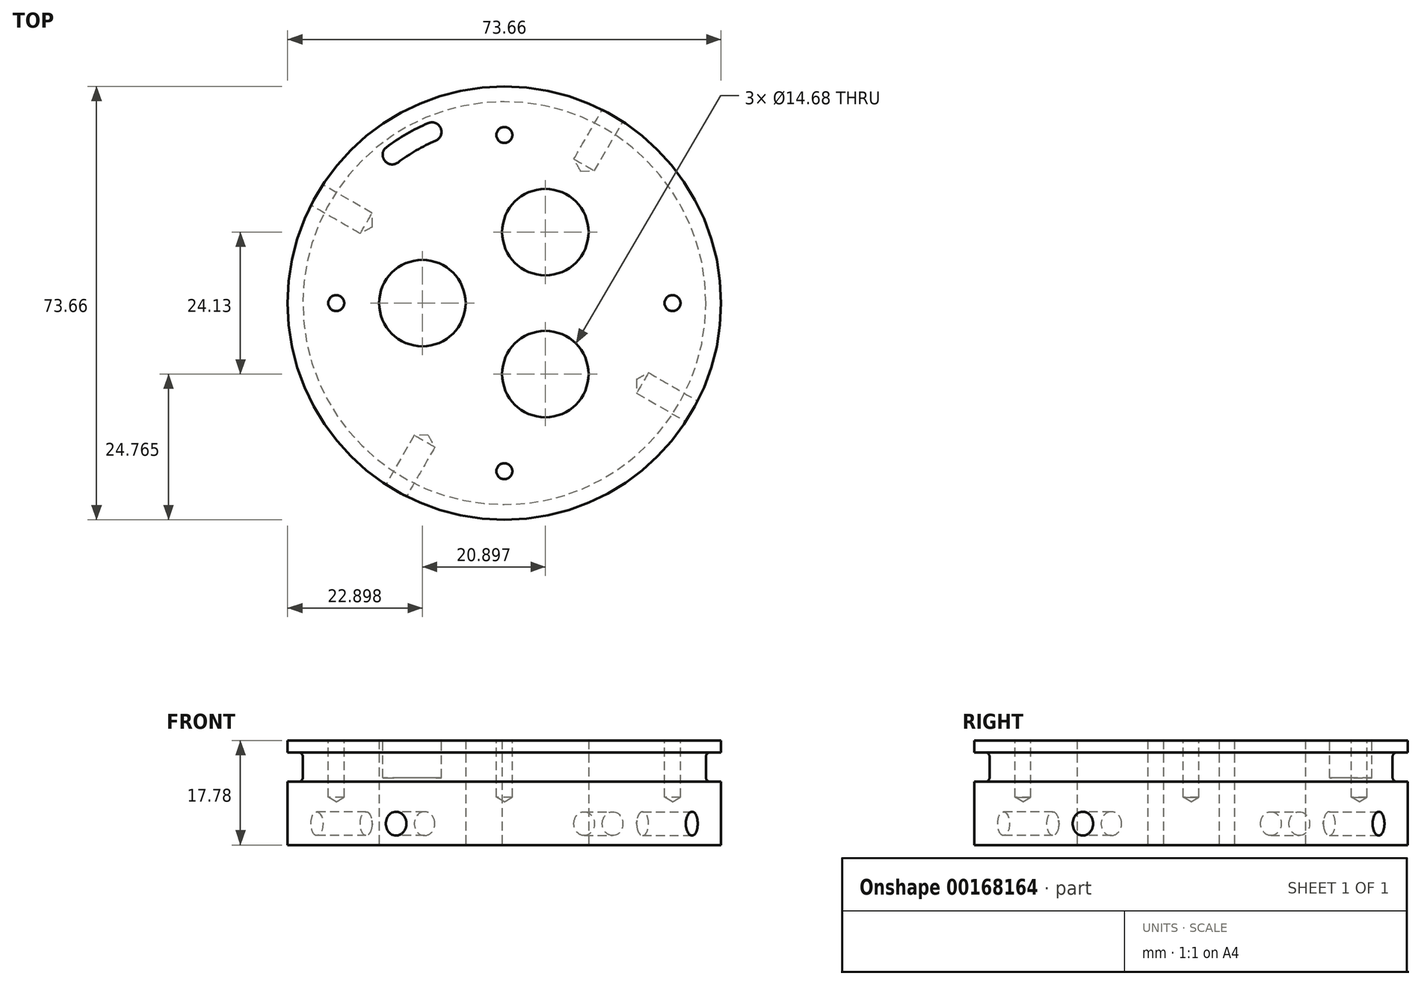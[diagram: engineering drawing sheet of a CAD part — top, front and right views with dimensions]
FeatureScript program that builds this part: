
annotation { "Feature Type Name" : "Feature", "Feature Type Description" : "" }
export const myFeature = defineFeature(function(context is Context, id is Id, definition is map)
    precondition{}
    {
        {
            var Q0;
            Q0=qCreatedBy(makeId("Top.planeOp"),FACE);
            var sketch = newSketch(context, id + "F0", { "sketchPlane" : qUnion([Q0])});
            skCircle(sketch, "E0", {"center": v(0, 0) * mm, "radius": 36.83 * mm});
            skSolve(sketch);
        }
        {
            var Q0;
            Q0=makeQuery(id+"F0.imprint","IMPRINT",FACE,{"disambiguationData":[TD([[makeQuery(id+"F0.imprint","IMPRINT",EDGE,{"derivedFrom":sQuery(id+"F0.wireOp",EDGE,"E0")}),1.0]])]});
            extrude(context, id + "F1", {"entities" : qUnion([Q0]), "depth" : 17.78 * mm});
        }
        {
            var Q0;
            {var subQ0=makeQuery(id+"FhJubWmbG7UBd7M_1.boolean.opBoolean","COPY",FACE,{"derivedFrom":makeQuery(id+"FhJubWmbG7UBd7M_1.opExtrude","SWEPT_FACE",FACE,{"disambiguationData":[OSD([sQuery(id+"FRuIeaWD6VeLny9_1.wireOp",EDGE,"idePJaX5-tPPE-BKw2-N1m4-zZUQrY6AHjir")])]})});Q0=makeQuery(id+"FOQC5dfjhO448EJ_1.boolean.opBoolean","SPLIT",FACE,{"disambiguationData":[TD([subQ0])],"derivedFrom":makeQuery(id+"FkcieFRIapZdHPD_1.boolean.opBoolean","SPLIT",FACE,{"disambiguationData":[TD([subQ0])],"derivedFrom":makeQuery(id+"F1.opExtrude","CAP_FACE",FACE,{"disambiguationData":[OSD([sQuery(id+"F0.wireOp",EDGE,"E0")])],"isStart":false})})});}
            var sketch = newSketch(context, id + "F2", { "sketchPlane" : qUnion([Q0])});
            skCircle(sketch, "E1", {"center": v(0, 0) * mm, "radius": 28.58 * mm, "construction": true});
            skLineSegment(sketch, "E2", {"start": v(0, 0) * mm, "end": v(28.57, 0) * mm, "construction": true});
            skPoint(sketch, "E3", {"position": v(28.58, 0) * mm});
            skPoint(sketch, "E4.1.0", {"position": v(0, 28.58) * mm});
            skPoint(sketch, "E4.2.0", {"position": v(-28.58, 0) * mm});
            skPoint(sketch, "E4.3.0", {"position": v(0, -28.58) * mm});
            skSolve(sketch);
        }
        {
            var Q0;
            Q0=sQuery(id+"F2.wireOp",VERTEX,"E3");
            var Q1;
            Q1=sQuery(id+"F2.wireOp",VERTEX,"E4.3.0");
            var Q2;
            Q2=sQuery(id+"F2.wireOp",VERTEX,"E4.2.0");
            var Q3;
            Q3=sQuery(id+"F2.wireOp",VERTEX,"E4.1.0");
            var Q4;
            Q4=makeQuery(id+"F1.opExtrude","SWEPT_BODY",BODY,{"disambiguationData":[OSD([sQuery(id+"F0.wireOp",EDGE,"E0")])]});
            hole(context, id + "F3", {"style" : HoleStyle.SIMPLE, "endStyle" : HoleEndStyle.BLIND, "standardTappedOrClearance" : lookupTablePath({ "standard" : "ANSI", "engagement" : "75%", "pitch" : "32 tpi", "size" : "#6", "type" : "Tapped" }), "standardBlindInLast" : lookupTablePath({ "standard" : "ANSI", "engagement" : "75%", "pitch" : "32 tpi", "size" : "#6", "type" : "Tapped" }), "holeDiameter" : 2.7 * mm, "holeDepth" : 9.65 * mm, "locations" : qUnion([Q0, Q1, Q2, Q3]), "scope" : qUnion([Q4]), "majorDiameter" : 3.5 * mm});
        }
        {
            var Q0;
            Q0=makeQuery(id+"FOQC5dfjhO448EJ_1.boolean.opBoolean","SPLIT",FACE,{"disambiguationData":[TD([makeQuery(id+"FhJubWmbG7UBd7M_1.boolean.opBoolean","COPY",FACE,{"derivedFrom":makeQuery(id+"FhJubWmbG7UBd7M_1.opExtrude","SWEPT_FACE",FACE,{"disambiguationData":[OSD([sQuery(id+"FRuIeaWD6VeLny9_1.wireOp",EDGE,"idePJaX5-tPPE-BKw2-N1m4-zZUQrY6AHjir")])]})})])],"derivedFrom":makeQuery(id+"F1.opExtrude","CAP_FACE",FACE,{"disambiguationData":[OSD([sQuery(id+"F0.wireOp",EDGE,"E0")])],"isStart":false})});
            cPlane(context, id + "F4", {"entities" : qUnion([Q0]), "cplaneType" : CPlaneType.OFFSET, "offset" : 2.03 * mm, "oppositeDirection" : true, "width" : 152.4 * mm, "height" : 152.4 * mm});
        }
        {
            var Q0;
            Q0=qCreatedBy(id+"F4.planeOp",FACE);
            var sketch = newSketch(context, id + "F5", { "sketchPlane" : qUnion([Q0])});
            skCircle(sketch, "E5", {"center": v(0, 0) * mm, "radius": 34.24 * mm});
            skCircle(sketch, "E6.0", {"center": v(0, 0) * mm, "radius": 36.83 * mm});
            skSolve(sketch);
        }
        {
            var Q0;
            Q0=qSketchRegion(id+"F5",true);
            extrude(context, id + "F6", {"entities" : qUnion([Q0]), "operationType" : NewBodyOperationType.REMOVE, "oppositeDirection" : true, "depth" : 5 * mm});
        }
        {
            var Q0;
            Q0=makeQuery(id+"F6.boolean.opBoolean","COPY",EDGE,{"derivedFrom":makeQuery(id+"F6.opExtrude","CAP_EDGE",EDGE,{"disambiguationData":[OSD([sQuery(id+"F5.wireOp",EDGE,"E5")])],"isStart":false})});
            var Q1;
            Q1=makeQuery(id+"F6.boolean.opBoolean","COPY",EDGE,{"derivedFrom":makeQuery(id+"F6.opExtrude","CAP_EDGE",EDGE,{"disambiguationData":[OSD([sQuery(id+"F5.wireOp",EDGE,"E5")])],"isStart":true})});
            fillet(context, id + "F7", {"entities" : qUnion([Q0, Q1]), "radius" : 0.76 * mm, "tangentPropagation" : true, "allowEdgeOverflow" : false});
        }
        {
            var Q0;
            {var subQ1=sQuery(id+"F0.wireOp",EDGE,"E0");var subQ2=makeQuery(id+"F1.opExtrude","SWEPT_FACE",FACE,{"disambiguationData":[OSD([subQ1])]});Q0=makeQuery(id+"FkcieFRIapZdHPD_1.boolean.opBoolean","SPLIT",FACE,{"disambiguationData":[TD([subQ2])],"derivedFrom":makeQuery(id+"F1.opExtrude","CAP_FACE",FACE,{"disambiguationData":[OSD([subQ1])],"isStart":false})});}
            var sketch = newSketch(context, id + "F8", { "sketchPlane" : qUnion([Q0])});
            skCircle(sketch, "E7.0", {"center": v(0, 0) * mm, "radius": 36.83 * mm, "construction": true});
            skPoint(sketch, "E8", {"position": v(-18.41, -31.9) * mm});
            skLineSegment(sketch, "E9", {"start": v(0, -36.83) * mm, "end": v(0, 0) * mm, "construction": true});
            skLineSegment(sketch, "E10", {"start": v(0, 0) * mm, "end": v(-17.96, -31.1) * mm, "construction": true});
            skLineSegment(sketch, "E11", {"start": v(-17.96, -31.1) * mm, "end": v(-18.41, -31.9) * mm, "construction": true});
            skLineSegment(sketch, "E12", {"start": v(0, 0) * mm, "end": v(18.41, 31.9) * mm, "construction": true});
            skLineSegment(sketch, "E13", {"start": v(18.41, 31.9) * mm, "end": v(0, 0) * mm, "construction": true});
            skLineSegment(sketch, "E14", {"start": v(31.9, -18.41) * mm, "end": v(0, 0) * mm, "construction": true});
            skLineSegment(sketch, "E15", {"start": v(0, 0) * mm, "end": v(-31.9, 18.41) * mm, "construction": true});
            skPoint(sketch, "E16", {"position": v(18.41, 31.9) * mm});
            skPoint(sketch, "E17", {"position": v(31.9, -18.41) * mm});
            skPoint(sketch, "E18", {"position": v(-31.9, 18.41) * mm});
            skSolve(sketch);
        }
        {
            var Q0;
            Q0=qCreatedBy(makeId("Front.planeOp"),FACE);
            var sketch = newSketch(context, id + "F9", { "sketchPlane" : qUnion([Q0])});
            skLineSegment(sketch, "E19", {"start": v(0, 0) * mm, "end": v(0, 38.57) * mm, "construction": true});
            skSolve(sketch);
        }
        {
            var Q0;
            Q0=sQuery(id+"F9.wireOp",EDGE,"E19");
            cPlane(context, id + "F10", {"entities" : qUnion([Q0]), "cplaneType" : CPlaneType.LINE_ANGLE, "offset" : 25.4 * mm, "angle" : 60 * degree, "width" : 152.4 * mm, "height" : 152.4 * mm});
        }
        {
            var Q0;
            Q0=sQuery(id+"F8.wireOp",VERTEX,"E8");
            var Q1;
            Q1=qCreatedBy(id+"F10.planeOp",FACE);
            cPlane(context, id + "F11", {"entities" : qUnion([Q0, Q1]), "cplaneType" : CPlaneType.PLANE_POINT, "offset" : 25.4 * mm, "width" : 152.4 * mm, "height" : 152.4 * mm});
        }
        {
            var Q0;
            Q0=qCreatedBy(id+"F11.planeOp",FACE);
            var Q1;
            Q1=sQuery(id+"F8.wireOp",VERTEX,"E16");
            cPlane(context, id + "F12", {"entities" : qUnion([Q0, Q1]), "cplaneType" : CPlaneType.PLANE_POINT, "offset" : 25.4 * mm, "width" : 152.4 * mm, "height" : 152.4 * mm});
        }
        {
            var Q0;
            Q0=sQuery(id+"F9.wireOp",EDGE,"E19");
            cPlane(context, id + "F13", {"entities" : qUnion([Q0]), "cplaneType" : CPlaneType.LINE_ANGLE, "offset" : 25.4 * mm, "angle" : 150 * degree, "width" : 152.4 * mm, "height" : 152.4 * mm});
        }
        {
            var Q0;
            Q0=sQuery(id+"F8.wireOp",VERTEX,"E18");
            var Q1;
            Q1=qCreatedBy(id+"F13.planeOp",FACE);
            cPlane(context, id + "F14", {"entities" : qUnion([Q0, Q1]), "cplaneType" : CPlaneType.PLANE_POINT, "offset" : 25.4 * mm, "width" : 152.4 * mm, "height" : 152.4 * mm});
        }
        {
            var Q0;
            Q0=qCreatedBy(id+"F13.planeOp",FACE);
            var Q1;
            Q1=sQuery(id+"F8.wireOp",VERTEX,"E17");
            cPlane(context, id + "F15", {"entities" : qUnion([Q0, Q1]), "cplaneType" : CPlaneType.PLANE_POINT, "offset" : 25.4 * mm, "width" : 152.4 * mm, "height" : 152.4 * mm});
        }
        {
            var Q0;
            Q0=qCreatedBy(id+"F11.planeOp",FACE);
            var sketch = newSketch(context, id + "F16", { "sketchPlane" : qUnion([Q0])});
            skLineSegment(sketch, "E20", {"start": v(0, 0) * mm, "end": v(0, 3.63) * mm, "construction": true});
            skPoint(sketch, "E21", {"position": v(0, 3.63) * mm});
            skSolve(sketch);
        }
        {
            var Q0;
            Q0=qCreatedBy(id+"F12.planeOp",FACE);
            var sketch = newSketch(context, id + "F17", { "sketchPlane" : qUnion([Q0])});
            skPoint(sketch, "E22", {"position": v(0, 3.63) * mm});
            skLineSegment(sketch, "E23.0", {"start": v(0, 0) * mm, "end": v(0, 3.63) * mm, "construction": true});
            skSolve(sketch);
        }
        {
            var Q0;
            Q0=qCreatedBy(id+"F14.planeOp",FACE);
            var sketch = newSketch(context, id + "F18", { "sketchPlane" : qUnion([Q0])});
            skLineSegment(sketch, "E24", {"start": v(0, 0) * mm, "end": v(0, 3.63) * mm, "construction": true});
            skLineSegment(sketch, "E25.0", {"start": v(-36.83, 0) * mm, "end": v(-36.83, 3.63) * mm, "construction": true});
            skPoint(sketch, "E26", {"position": v(0, 3.63) * mm});
            skLineSegment(sketch, "E27", {"start": v(-36.83, 3.63) * mm, "end": v(0, 3.63) * mm, "construction": true});
            skSolve(sketch);
        }
        {
            var Q0;
            Q0=qCreatedBy(id+"F15.planeOp",FACE);
            var sketch = newSketch(context, id + "F19", { "sketchPlane" : qUnion([Q0])});
            skLineSegment(sketch, "E28.0", {"start": v(0, 0) * mm, "end": v(0, 3.63) * mm, "construction": true});
            skPoint(sketch, "E29", {"position": v(0, 3.63) * mm});
            skSolve(sketch);
        }
        {
            var Q0;
            Q0=sQuery(id+"F19.wireOp",VERTEX,"E29");
            var Q1;
            Q1=makeQuery(id+"F1.opExtrude","SWEPT_BODY",BODY,{"disambiguationData":[OSD([sQuery(id+"F0.wireOp",EDGE,"E0")])]});
            hole(context, id + "F20", {"style" : HoleStyle.SIMPLE, "endStyle" : HoleEndStyle.BLIND, "oppositeDirection" : true, "standardTappedOrClearance" : lookupTablePath({ "standard" : "ANSI", "engagement" : "75%", "pitch" : "32 tpi", "size" : "#10", "type" : "Tapped" }), "standardBlindInLast" : lookupTablePath({ "standard" : "ANSI", "engagement" : "75%", "pitch" : "32 tpi", "size" : "#10", "type" : "Tapped" }), "holeDiameter" : 4.04 * mm, "holeDepth" : 9.65 * mm, "locations" : qUnion([Q0]), "scope" : qUnion([Q1]), "majorDiameter" : 4.83 * mm});
        }
        {
            var Q0;
            Q0=sQuery(id+"F18.wireOp",VERTEX,"E26");
            var Q1;
            Q1=makeQuery(id+"F1.opExtrude","SWEPT_BODY",BODY,{"disambiguationData":[OSD([sQuery(id+"F0.wireOp",EDGE,"E0")])]});
            hole(context, id + "F21", {"style" : HoleStyle.SIMPLE, "endStyle" : HoleEndStyle.BLIND, "standardTappedOrClearance" : lookupTablePath({ "standard" : "ANSI", "engagement" : "75%", "pitch" : "32 tpi", "size" : "#10", "type" : "Tapped" }), "standardBlindInLast" : lookupTablePath({ "standard" : "ANSI", "engagement" : "75%", "pitch" : "32 tpi", "size" : "#10", "type" : "Tapped" }), "holeDiameter" : 4.04 * mm, "holeDepth" : 9.65 * mm, "locations" : qUnion([Q0]), "scope" : qUnion([Q1]), "majorDiameter" : 4.83 * mm});
        }
        {
            var Q0;
            Q0=sQuery(id+"F16.wireOp",VERTEX,"E21");
            var Q1;
            Q1=makeQuery(id+"F1.opExtrude","SWEPT_BODY",BODY,{"disambiguationData":[OSD([sQuery(id+"F0.wireOp",EDGE,"E0")])]});
            hole(context, id + "F22", {"style" : HoleStyle.SIMPLE, "endStyle" : HoleEndStyle.BLIND, "oppositeDirection" : true, "standardTappedOrClearance" : lookupTablePath({ "standard" : "ANSI", "engagement" : "75%", "pitch" : "32 tpi", "size" : "#10", "type" : "Tapped" }), "standardBlindInLast" : lookupTablePath({ "standard" : "ANSI", "engagement" : "75%", "pitch" : "32 tpi", "size" : "#10", "type" : "Tapped" }), "holeDiameter" : 4.04 * mm, "holeDepth" : 9.65 * mm, "locations" : qUnion([Q0]), "scope" : qUnion([Q1]), "majorDiameter" : 4.83 * mm});
        }
        {
            var Q0;
            Q0=sQuery(id+"F17.wireOp",VERTEX,"E22");
            var Q1;
            Q1=makeQuery(id+"F1.opExtrude","SWEPT_BODY",BODY,{"disambiguationData":[OSD([sQuery(id+"F0.wireOp",EDGE,"E0")])]});
            hole(context, id + "F23", {"style" : HoleStyle.SIMPLE, "endStyle" : HoleEndStyle.BLIND, "standardTappedOrClearance" : lookupTablePath({ "standard" : "ANSI", "engagement" : "75%", "pitch" : "32 tpi", "size" : "#10", "type" : "Tapped" }), "standardBlindInLast" : lookupTablePath({ "standard" : "ANSI", "engagement" : "75%", "pitch" : "32 tpi", "size" : "#10", "type" : "Tapped" }), "holeDiameter" : 4.04 * mm, "holeDepth" : 9.65 * mm, "locations" : qUnion([Q0]), "scope" : qUnion([Q1]), "majorDiameter" : 4.83 * mm});
        }
        {
            var Q0;
            Q0=makeQuery(id+"F1.opExtrude","CAP_FACE",FACE,{"disambiguationData":[OSD([sQuery(id+"F0.wireOp",EDGE,"E0")])],"isStart":true});
            var sketch = newSketch(context, id + "F24", { "sketchPlane" : qUnion([Q0])});
            skPoint(sketch, "E30", {"position": v(-13.93, 0) * mm});
            skPoint(sketch, "E31.1.0", {"position": v(6.97, -12.07) * mm});
            skPoint(sketch, "E31.2.0", {"position": v(6.97, 12.07) * mm});
            skPoint(sketch, "E31.center", {"position": v(0, 0) * mm});
            skSolve(sketch);
        }
        {
            var Q0;
            Q0=sQuery(id+"F24.wireOp",VERTEX,"4a09c47b-9143-4afa-8474-e2cbf5050e91");
            var Q1;
            Q1=sQuery(id+"F24.wireOp",VERTEX,"E31.1.0");
            var Q2;
            Q2=sQuery(id+"F24.wireOp",VERTEX,"E30");
            var Q3;
            Q3=sQuery(id+"F24.wireOp",VERTEX,"E31.2.0");
            var Q4;
            Q4=makeQuery(id+"F1.opExtrude","SWEPT_BODY",BODY,{"disambiguationData":[OSD([sQuery(id+"F0.wireOp",EDGE,"E0")])]});
            hole(context, id + "F25", {"style" : HoleStyle.SIMPLE, "endStyle" : HoleEndStyle.THROUGH, "holeDiameter" : 14.68 * mm, "locations" : qUnion([Q0, Q1, Q2, Q3]), "scope" : qUnion([Q4]), "isTappedThrough" : true});
        }
        {
            var Q0;
            Q0=makeQuery(id+"F1.opExtrude","CAP_FACE",FACE,{"disambiguationData":[OSD([sQuery(id+"F0.wireOp",EDGE,"E0")])],"isStart":false});
            var sketch = newSketch(context, id + "F26", { "sketchPlane" : qUnion([Q0])});
            skCircle(sketch, "E32.0", {"center": v(0, 0) * mm, "radius": 34.24 * mm, "construction": true});
            skCircle(sketch, "E33", {"center": v(0, 0) * mm, "radius": 29.97 * mm, "construction": true});
            skCircle(sketch, "E34.0", {"center": v(0, 0) * mm, "radius": 33.22 * mm, "construction": true});
            skArc(sketch, "E35", {"start": v(-10.25, 28.16) * mm, "mid": v(-14.99, 25.96) * mm, "end": v(-19.27, 22.96) * mm});
            skLineSegment(sketch, "E36", {"start": v(-14.99, 25.96) * mm, "end": v(0, 0) * mm, "construction": true});
            skArc(sketch, "E37", {"start": v(-21.36, 25.45) * mm, "mid": v(-16.61, 28.77) * mm, "end": v(-11.36, 31.22) * mm});
            skLineSegment(sketch, "E38", {"start": v(-11.36, 31.22) * mm, "end": v(-10.25, 28.16) * mm});
            skLineSegment(sketch, "E39", {"start": v(-21.36, 25.45) * mm, "end": v(-19.27, 22.96) * mm});
            skLineSegment(sketch, "E40", {"start": v(0, 0) * mm, "end": v(-19.27, 22.96) * mm, "construction": true});
            skLineSegment(sketch, "E41", {"start": v(0, 0) * mm, "end": v(-10.25, 28.16) * mm, "construction": true});
            skSolve(sketch);
        }
        {
            var Q0;
            Q0=qSketchRegion(id+"F26",true);
            extrude(context, id + "F27", {"entities" : qUnion([Q0]), "operationType" : NewBodyOperationType.REMOVE, "oppositeDirection" : true, "depth" : 6.35 * mm});
        }
        {
            var Q0;
            Q0=makeQuery(id+"F27.boolean.opBoolean","COPY",EDGE,{"derivedFrom":makeQuery(id+"F27.opExtrude","SWEPT_EDGE",EDGE,{"disambiguationData":[OSD([sQuery(id+"F26.wireOp",EDGE,"E37"),sQuery(id+"F26.wireOp",EDGE,"E38")])]})});
            var Q1;
            Q1=makeQuery(id+"F27.boolean.opBoolean","COPY",EDGE,{"derivedFrom":makeQuery(id+"F27.opExtrude","SWEPT_EDGE",EDGE,{"disambiguationData":[OSD([sQuery(id+"F26.wireOp",EDGE,"E37"),sQuery(id+"F26.wireOp",EDGE,"E39")])]})});
            var Q2;
            Q2=makeQuery(id+"F27.boolean.opBoolean","COPY",EDGE,{"derivedFrom":makeQuery(id+"F27.opExtrude","SWEPT_EDGE",EDGE,{"disambiguationData":[OSD([sQuery(id+"F26.wireOp",EDGE,"E35"),sQuery(id+"F26.wireOp",EDGE,"E39")])]})});
            var Q3;
            Q3=makeQuery(id+"F27.boolean.opBoolean","COPY",EDGE,{"derivedFrom":makeQuery(id+"F27.opExtrude","SWEPT_EDGE",EDGE,{"disambiguationData":[OSD([sQuery(id+"F26.wireOp",EDGE,"E35"),sQuery(id+"F26.wireOp",EDGE,"E38")])]})});
            fillet(context, id + "F28", {"entities" : qUnion([Q0, Q1, Q2, Q3]), "radius" : 1.59 * mm, "tangentPropagation" : true, "allowEdgeOverflow" : false});
        }
    });
